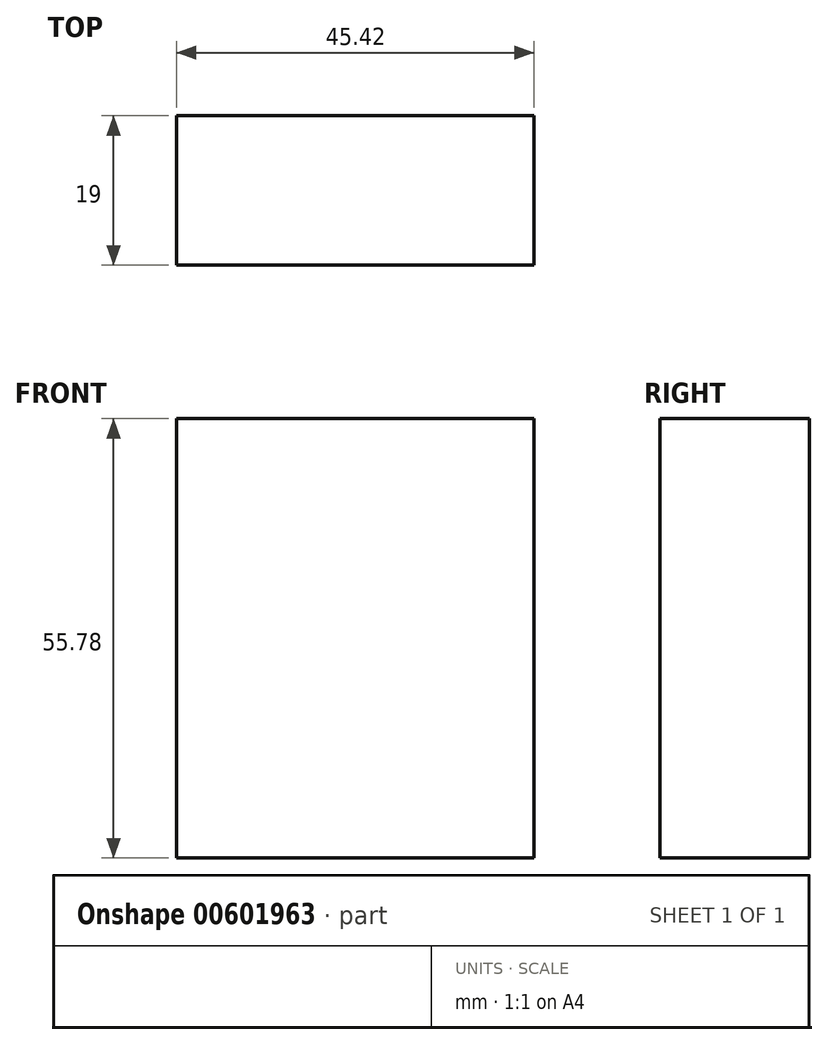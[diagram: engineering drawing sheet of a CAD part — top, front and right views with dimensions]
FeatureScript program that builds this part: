
annotation { "Feature Type Name" : "Feature", "Feature Type Description" : "" }
export const myFeature = defineFeature(function(context is Context, id is Id, definition is map)
    precondition{}
    {
        {
            var Q0;
            Q0=qCreatedBy(makeId("Front.planeOp"),FACE);
            var sketch = newSketch(context, id + "F0", { "sketchPlane" : qUnion([Q0])});
            skLineSegment(sketch, "E0", {"start": v(-34.3, 28.65) * mm, "end": v(11.13, 28.65) * mm});
            skLineSegment(sketch, "E1", {"start": v(-34.3, 28.65) * mm, "end": v(-34.3, -27.13) * mm});
            skLineSegment(sketch, "E2", {"start": v(11.13, 28.65) * mm, "end": v(11.13, -27.13) * mm});
            skLineSegment(sketch, "E3", {"start": v(-34.3, -27.13) * mm, "end": v(11.13, -27.13) * mm});
            skSolve(sketch);
        }
        {
            var Q0;
            Q0=makeQuery(id+"F0.imprint","IMPRINT",FACE,{"disambiguationData":[TD([[makeQuery(id+"F0.imprint","IMPRINT",EDGE,{"derivedFrom":sQuery(id+"F0.wireOp",EDGE,"E0")}),-1.0]])]});
            extrude(context, id + "F1", {"entities" : qUnion([Q0]), "depth" : 19 * mm, "offsetDistance" : 25.4 * mm});
        }
    });
